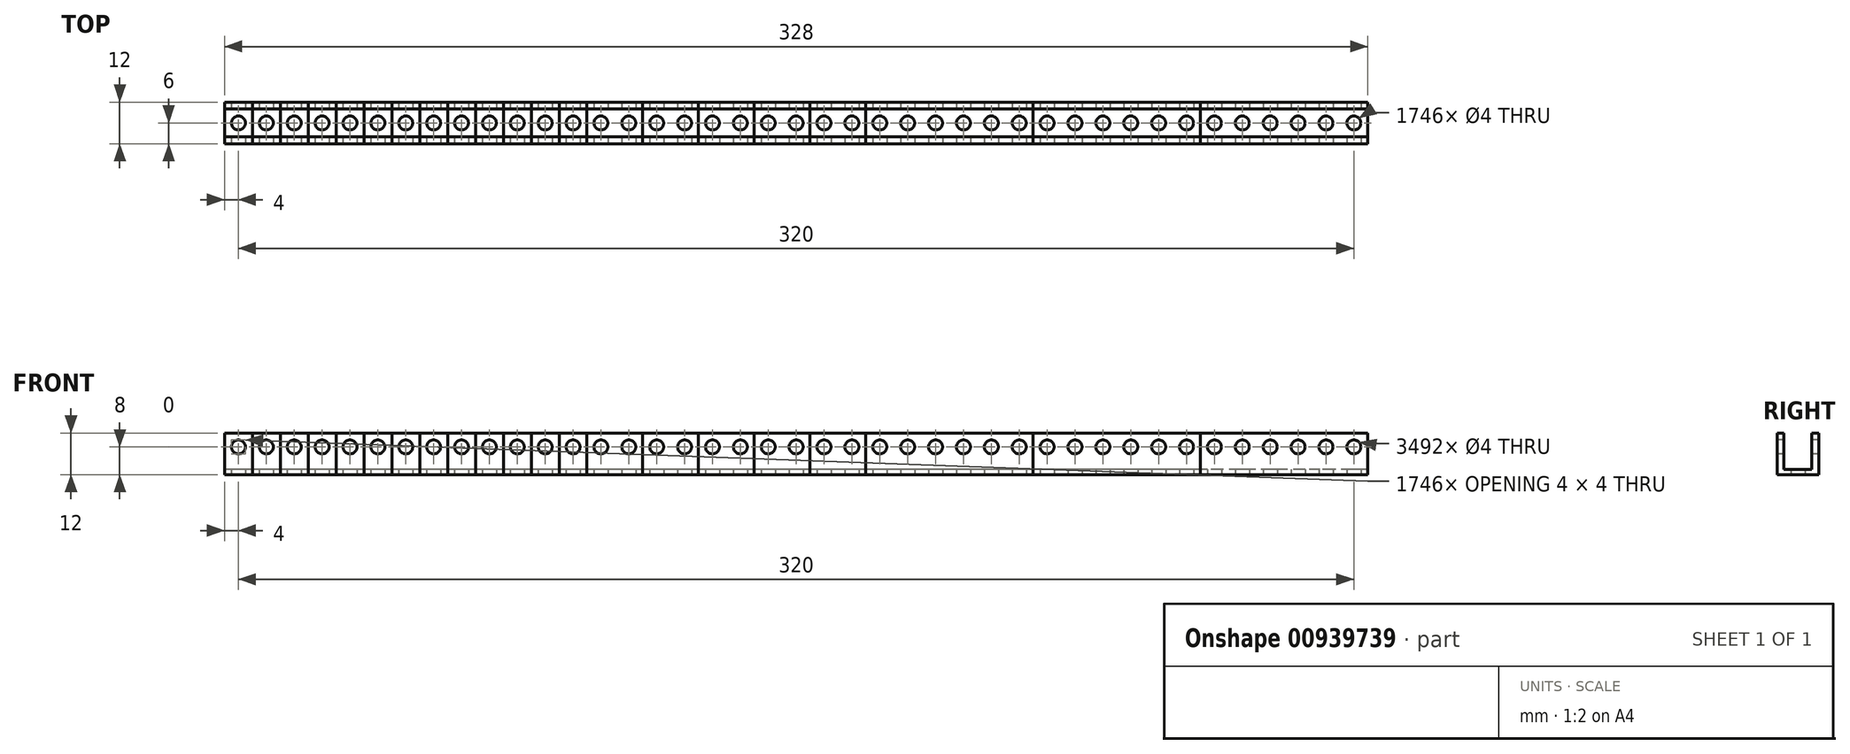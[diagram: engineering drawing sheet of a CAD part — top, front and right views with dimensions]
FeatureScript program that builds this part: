
annotation { "Feature Type Name" : "Feature", "Feature Type Description" : "" }
export const myFeature = defineFeature(function(context is Context, id is Id, definition is map)
    precondition{}
    {
        {
            var Q0;
            Q0=qCreatedBy(makeId("Right.planeOp"),FACE);
            var sketch = newSketch(context, id + "F0", { "sketchPlane" : qUnion([Q0])});
            skLineSegment(sketch, "E0.bottom", {"start": v(0, 0) * mm, "end": v(12, 0) * mm});
            skLineSegment(sketch, "E0.top", {"start": v(0, 12) * mm, "end": v(2, 12) * mm});
            skLineSegment(sketch, "E0.left", {"start": v(0, 0) * mm, "end": v(0, 12) * mm});
            skLineSegment(sketch, "E0.right", {"start": v(12, 0) * mm, "end": v(12, 12) * mm});
            skLineSegment(sketch, "E1.top", {"start": v(2, 1.5) * mm, "end": v(10, 1.5) * mm});
            skLineSegment(sketch, "E1.left", {"start": v(2, 12) * mm, "end": v(2, 1.5) * mm});
            skLineSegment(sketch, "E1.right", {"start": v(10, 12) * mm, "end": v(10, 1.5) * mm});
            skLineSegment(sketch, "E2.trimOffspring", {"start": v(10, 12) * mm, "end": v(12, 12) * mm});
            skSolve(sketch);
        }
        {
            var Q0;
            Q0=qSketchRegion(id+"F0",true);
            extrude(context, id + "F1", {"entities" : qUnion([Q0]), "depth" : 8 * mm, "offsetDistance" : 25 * mm});
        }
        {
            var Q0;
            Q0=qSketchRegion(id+"F0",true);
            extrude(context, id + "F2", {"entities" : qUnion([Q0]), "depth" : 16 * mm, "offsetDistance" : 25 * mm});
        }
        {
            var Q0;
            Q0=qSketchRegion(id+"F0",true);
            extrude(context, id + "F3", {"entities" : qUnion([Q0]), "depth" : 24 * mm, "offsetDistance" : 25 * mm});
        }
        {
            var Q0;
            Q0=qSketchRegion(id+"F0",true);
            extrude(context, id + "F4", {"entities" : qUnion([Q0]), "depth" : 32 * mm, "offsetDistance" : 25 * mm});
        }
        {
            var Q0;
            Q0=qSketchRegion(id+"F0",true);
            extrude(context, id + "F5", {"entities" : qUnion([Q0]), "depth" : 40 * mm, "offsetDistance" : 25 * mm});
        }
        {
            var Q0;
            Q0=qSketchRegion(id+"F0",true);
            extrude(context, id + "F6", {"entities" : qUnion([Q0]), "depth" : 48 * mm, "offsetDistance" : 25 * mm});
        }
        {
            var Q0;
            Q0=qSketchRegion(id+"F0",true);
            extrude(context, id + "F7", {"entities" : qUnion([Q0]), "depth" : 56 * mm, "offsetDistance" : 25 * mm});
        }
        {
            var Q0;
            Q0=qSketchRegion(id+"F0",true);
            extrude(context, id + "F8", {"entities" : qUnion([Q0]), "depth" : 64 * mm, "offsetDistance" : 25 * mm});
        }
        {
            var Q0;
            Q0=qSketchRegion(id+"F0",true);
            extrude(context, id + "F9", {"entities" : qUnion([Q0]), "depth" : 72 * mm, "offsetDistance" : 25 * mm});
        }
        {
            var Q0;
            Q0=qSketchRegion(id+"F0",true);
            extrude(context, id + "F10", {"entities" : qUnion([Q0]), "depth" : 80 * mm, "offsetDistance" : 25 * mm});
        }
        {
            var Q0;
            Q0=qSketchRegion(id+"F0",true);
            extrude(context, id + "F11", {"entities" : qUnion([Q0]), "depth" : 88 * mm, "offsetDistance" : 25 * mm});
        }
        {
            var Q0;
            Q0=qSketchRegion(id+"F0",true);
            extrude(context, id + "F12", {"entities" : qUnion([Q0]), "depth" : 96 * mm, "offsetDistance" : 25 * mm});
        }
        {
            var Q0;
            Q0=qSketchRegion(id+"F0",true);
            extrude(context, id + "F13", {"entities" : qUnion([Q0]), "depth" : 104 * mm, "offsetDistance" : 25 * mm});
        }
        {
            var Q0;
            Q0=qSketchRegion(id+"F0",true);
            extrude(context, id + "F14", {"entities" : qUnion([Q0]), "depth" : 120 * mm, "offsetDistance" : 25 * mm});
        }
        {
            var Q0;
            Q0=qSketchRegion(id+"F0",true);
            extrude(context, id + "F15", {"entities" : qUnion([Q0]), "depth" : 136 * mm, "offsetDistance" : 25 * mm});
        }
        {
            var Q0;
            Q0=qSketchRegion(id+"F0",true);
            extrude(context, id + "F16", {"entities" : qUnion([Q0]), "depth" : 152 * mm, "offsetDistance" : 25 * mm});
        }
        {
            var Q0;
            Q0=qSketchRegion(id+"F0",true);
            extrude(context, id + "F17", {"entities" : qUnion([Q0]), "depth" : 168 * mm, "offsetDistance" : 25 * mm});
        }
        {
            var Q0;
            Q0=qSketchRegion(id+"F0",true);
            extrude(context, id + "F18", {"entities" : qUnion([Q0]), "depth" : 184 * mm, "offsetDistance" : 25 * mm});
        }
        {
            var Q0;
            Q0=qSketchRegion(id+"F0",true);
            extrude(context, id + "F19", {"entities" : qUnion([Q0]), "depth" : 232 * mm, "offsetDistance" : 25 * mm});
        }
        {
            var Q0;
            Q0=qSketchRegion(id+"F0",true);
            extrude(context, id + "F20", {"entities" : qUnion([Q0]), "depth" : 280 * mm, "offsetDistance" : 25 * mm});
        }
        {
            var Q0;
            Q0=qSketchRegion(id+"F0",true);
            extrude(context, id + "F21", {"entities" : qUnion([Q0]), "depth" : 328 * mm, "offsetDistance" : 25 * mm});
        }
        {
            var Q0;
            Q0=qCreatedBy(makeId("Front.planeOp"),FACE);
            var sketch = newSketch(context, id + "F22", { "sketchPlane" : qUnion([Q0])});
            skLineSegment(sketch, "E3.bottom", {"start": v(0, 0) * mm, "end": v(4, 0) * mm, "construction": true});
            skLineSegment(sketch, "E3.top", {"start": v(0, 8) * mm, "end": v(4, 8) * mm, "construction": true});
            skLineSegment(sketch, "E3.left", {"start": v(0, 0) * mm, "end": v(0, 8) * mm, "construction": true});
            skLineSegment(sketch, "E3.right", {"start": v(4, 0) * mm, "end": v(4, 8) * mm, "construction": true});
            skCircle(sketch, "E4", {"center": v(4, 8) * mm, "radius": 2 * mm});
            skCircle(sketch, "E5.1.0.0", {"center": v(12, 8) * mm, "radius": 2 * mm});
            skCircle(sketch, "E5.2.0.0", {"center": v(20, 8) * mm, "radius": 2 * mm});
            skLineSegment(sketch, "E5.direction1", {"start": v(4, 8) * mm, "end": v(12, 8) * mm, "construction": true});
            skCircle(sketch, "E6.0.3.0", {"center": v(28, 8) * mm, "radius": 2 * mm});
            skCircle(sketch, "E6.0.4.0", {"center": v(36, 8) * mm, "radius": 2 * mm});
            skCircle(sketch, "E6.0.5.0", {"center": v(44, 8) * mm, "radius": 2 * mm});
            skCircle(sketch, "E6.0.6.0", {"center": v(52, 8) * mm, "radius": 2 * mm});
            skCircle(sketch, "E6.0.7.0", {"center": v(60, 8) * mm, "radius": 2 * mm});
            skCircle(sketch, "E6.0.8.0", {"center": v(68, 8) * mm, "radius": 2 * mm});
            skCircle(sketch, "E6.0.9.0", {"center": v(76, 8) * mm, "radius": 2 * mm});
            skCircle(sketch, "E6.0.10.0", {"center": v(84, 8) * mm, "radius": 2 * mm});
            skCircle(sketch, "E6.0.11.0", {"center": v(92, 8) * mm, "radius": 2 * mm});
            skCircle(sketch, "E6.0.12.0", {"center": v(100, 8) * mm, "radius": 2 * mm});
            skCircle(sketch, "E6.0.13.0", {"center": v(108, 8) * mm, "radius": 2 * mm});
            skCircle(sketch, "E6.0.14.0", {"center": v(116, 8) * mm, "radius": 2 * mm});
            skCircle(sketch, "E6.0.15.0", {"center": v(124, 8) * mm, "radius": 2 * mm});
            skCircle(sketch, "E6.0.16.0", {"center": v(132, 8) * mm, "radius": 2 * mm});
            skCircle(sketch, "E6.0.17.0", {"center": v(140, 8) * mm, "radius": 2 * mm});
            skCircle(sketch, "E6.0.18.0", {"center": v(148, 8) * mm, "radius": 2 * mm});
            skCircle(sketch, "E6.0.19.0", {"center": v(156, 8) * mm, "radius": 2 * mm});
            skCircle(sketch, "E6.0.20.0", {"center": v(164, 8) * mm, "radius": 2 * mm});
            skCircle(sketch, "E6.0.21.0", {"center": v(172, 8) * mm, "radius": 2 * mm});
            skCircle(sketch, "E6.0.22.0", {"center": v(180, 8) * mm, "radius": 2 * mm});
            skCircle(sketch, "E6.0.23.0", {"center": v(188, 8) * mm, "radius": 2 * mm});
            skCircle(sketch, "E6.0.24.0", {"center": v(196, 8) * mm, "radius": 2 * mm});
            skCircle(sketch, "E6.0.25.0", {"center": v(204, 8) * mm, "radius": 2 * mm});
            skCircle(sketch, "E6.0.26.0", {"center": v(212, 8) * mm, "radius": 2 * mm});
            skCircle(sketch, "E6.0.27.0", {"center": v(220, 8) * mm, "radius": 2 * mm});
            skCircle(sketch, "E6.0.28.0", {"center": v(228, 8) * mm, "radius": 2 * mm});
            skCircle(sketch, "E6.0.29.0", {"center": v(236, 8) * mm, "radius": 2 * mm});
            skCircle(sketch, "E6.0.30.0", {"center": v(244, 8) * mm, "radius": 2 * mm});
            skCircle(sketch, "E6.0.31.0", {"center": v(252, 8) * mm, "radius": 2 * mm});
            skCircle(sketch, "E6.0.32.0", {"center": v(260, 8) * mm, "radius": 2 * mm});
            skCircle(sketch, "E6.0.33.0", {"center": v(268, 8) * mm, "radius": 2 * mm});
            skCircle(sketch, "E6.0.34.0", {"center": v(276, 8) * mm, "radius": 2 * mm});
            skCircle(sketch, "E6.0.35.0", {"center": v(284, 8) * mm, "radius": 2 * mm});
            skCircle(sketch, "E6.0.36.0", {"center": v(292, 8) * mm, "radius": 2 * mm});
            skCircle(sketch, "E6.0.37.0", {"center": v(300, 8) * mm, "radius": 2 * mm});
            skCircle(sketch, "E6.0.38.0", {"center": v(308, 8) * mm, "radius": 2 * mm});
            skCircle(sketch, "E6.0.39.0", {"center": v(316, 8) * mm, "radius": 2 * mm});
            skCircle(sketch, "E6.0.40.0", {"center": v(324, 8) * mm, "radius": 2 * mm});
            skSolve(sketch);
        }
        {
            var Q0;
            Q0=qSketchRegion(id+"F22",true);
            extrude(context, id + "F23", {"entities" : qUnion([Q0]), "operationType" : NewBodyOperationType.REMOVE, "endBound" : BoundingType.THROUGH_ALL, "oppositeDirection" : true, "depth" : 25 * mm, "offsetDistance" : 25 * mm});
        }
        {
            var Q0;
            Q0=qCreatedBy(makeId("Top.planeOp"),FACE);
            var sketch = newSketch(context, id + "F24", { "sketchPlane" : qUnion([Q0])});
            skPoint(sketch, "E7.0", {"position": v(0, 12) * mm});
            skLineSegment(sketch, "E8.bottom", {"start": v(0, 12) * mm, "end": v(4, 12) * mm, "construction": true});
            skLineSegment(sketch, "E8.top", {"start": v(0, 0) * mm, "end": v(4, 0) * mm, "construction": true});
            skLineSegment(sketch, "E8.left", {"start": v(0, 12) * mm, "end": v(0, 0) * mm, "construction": true});
            skLineSegment(sketch, "E8.right", {"start": v(4, 12) * mm, "end": v(4, 0) * mm, "construction": true});
            skCircle(sketch, "E9", {"center": v(4, 6) * mm, "radius": 2 * mm});
            skCircle(sketch, "E10.1.0.0", {"center": v(12, 6) * mm, "radius": 2 * mm});
            skCircle(sketch, "E10.2.0.0", {"center": v(20, 6) * mm, "radius": 2 * mm});
            skCircle(sketch, "E10.3.0.0", {"center": v(28, 6) * mm, "radius": 2 * mm});
            skCircle(sketch, "E10.4.0.0", {"center": v(36, 6) * mm, "radius": 2 * mm});
            skCircle(sketch, "E10.5.0.0", {"center": v(44, 6) * mm, "radius": 2 * mm});
            skCircle(sketch, "E10.6.0.0", {"center": v(52, 6) * mm, "radius": 2 * mm});
            skCircle(sketch, "E10.7.0.0", {"center": v(60, 6) * mm, "radius": 2 * mm});
            skCircle(sketch, "E10.8.0.0", {"center": v(68, 6) * mm, "radius": 2 * mm});
            skCircle(sketch, "E10.9.0.0", {"center": v(76, 6) * mm, "radius": 2 * mm});
            skCircle(sketch, "E10.10.0.0", {"center": v(84, 6) * mm, "radius": 2 * mm});
            skCircle(sketch, "E10.11.0.0", {"center": v(92, 6) * mm, "radius": 2 * mm});
            skCircle(sketch, "E10.12.0.0", {"center": v(100, 6) * mm, "radius": 2 * mm});
            skCircle(sketch, "E10.13.0.0", {"center": v(108, 6) * mm, "radius": 2 * mm});
            skCircle(sketch, "E10.14.0.0", {"center": v(116, 6) * mm, "radius": 2 * mm});
            skCircle(sketch, "E10.15.0.0", {"center": v(124, 6) * mm, "radius": 2 * mm});
            skCircle(sketch, "E10.16.0.0", {"center": v(132, 6) * mm, "radius": 2 * mm});
            skCircle(sketch, "E10.17.0.0", {"center": v(140, 6) * mm, "radius": 2 * mm});
            skCircle(sketch, "E10.18.0.0", {"center": v(148, 6) * mm, "radius": 2 * mm});
            skCircle(sketch, "E10.19.0.0", {"center": v(156, 6) * mm, "radius": 2 * mm});
            skCircle(sketch, "E10.20.0.0", {"center": v(164, 6) * mm, "radius": 2 * mm});
            skCircle(sketch, "E10.21.0.0", {"center": v(172, 6) * mm, "radius": 2 * mm});
            skCircle(sketch, "E10.22.0.0", {"center": v(180, 6) * mm, "radius": 2 * mm});
            skCircle(sketch, "E10.23.0.0", {"center": v(188, 6) * mm, "radius": 2 * mm});
            skCircle(sketch, "E10.24.0.0", {"center": v(196, 6) * mm, "radius": 2 * mm});
            skCircle(sketch, "E10.25.0.0", {"center": v(204, 6) * mm, "radius": 2 * mm});
            skCircle(sketch, "E10.26.0.0", {"center": v(212, 6) * mm, "radius": 2 * mm});
            skCircle(sketch, "E10.27.0.0", {"center": v(220, 6) * mm, "radius": 2 * mm});
            skCircle(sketch, "E10.28.0.0", {"center": v(228, 6) * mm, "radius": 2 * mm});
            skCircle(sketch, "E10.29.0.0", {"center": v(236, 6) * mm, "radius": 2 * mm});
            skCircle(sketch, "E10.30.0.0", {"center": v(244, 6) * mm, "radius": 2 * mm});
            skCircle(sketch, "E10.31.0.0", {"center": v(252, 6) * mm, "radius": 2 * mm});
            skCircle(sketch, "E10.32.0.0", {"center": v(260, 6) * mm, "radius": 2 * mm});
            skCircle(sketch, "E10.33.0.0", {"center": v(268, 6) * mm, "radius": 2 * mm});
            skCircle(sketch, "E10.34.0.0", {"center": v(276, 6) * mm, "radius": 2 * mm});
            skCircle(sketch, "E10.35.0.0", {"center": v(284, 6) * mm, "radius": 2 * mm});
            skCircle(sketch, "E10.36.0.0", {"center": v(292, 6) * mm, "radius": 2 * mm});
            skCircle(sketch, "E10.37.0.0", {"center": v(300, 6) * mm, "radius": 2 * mm});
            skCircle(sketch, "E10.38.0.0", {"center": v(308, 6) * mm, "radius": 2 * mm});
            skCircle(sketch, "E10.39.0.0", {"center": v(316, 6) * mm, "radius": 2 * mm});
            skCircle(sketch, "E10.40.0.0", {"center": v(324, 6) * mm, "radius": 2 * mm});
            skLineSegment(sketch, "E10.direction1", {"start": v(4, 6) * mm, "end": v(12, 6) * mm, "construction": true});
            skSolve(sketch);
        }
        {
            var Q0;
            Q0=qSketchRegion(id+"F24",true);
            extrude(context, id + "F25", {"entities" : qUnion([Q0]), "operationType" : NewBodyOperationType.REMOVE, "endBound" : BoundingType.THROUGH_ALL, "depth" : 25 * mm, "offsetDistance" : 25 * mm});
        }
    });
